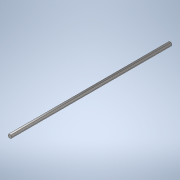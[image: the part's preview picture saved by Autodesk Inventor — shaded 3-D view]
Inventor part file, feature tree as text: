
AUTODESK INVENTOR PART (.ipt)
format: ipt  version: 2020 (Build 240168000, 168)  size: 107,520 bytes
history: native  units: in
note: dims shown in document units (in); Inventor stores cm internally (conversion verified against a paired STEP export)
features: extrude x1, sketch x1
ambient origin geometry x8: Origin, YZ Plane, XZ Plane, XY Plane, X Axis, Y Axis, Z Axis, Center Point
bodies: Solid1 (feature_tree)
feature tree (2):
  extrude  "Extrusion1"  Depth=25.0in TaperAngle=0.0deg
  sketch  "Sketch1"  dims[d0=0.5in d1=25.0in d2=0.0in]
